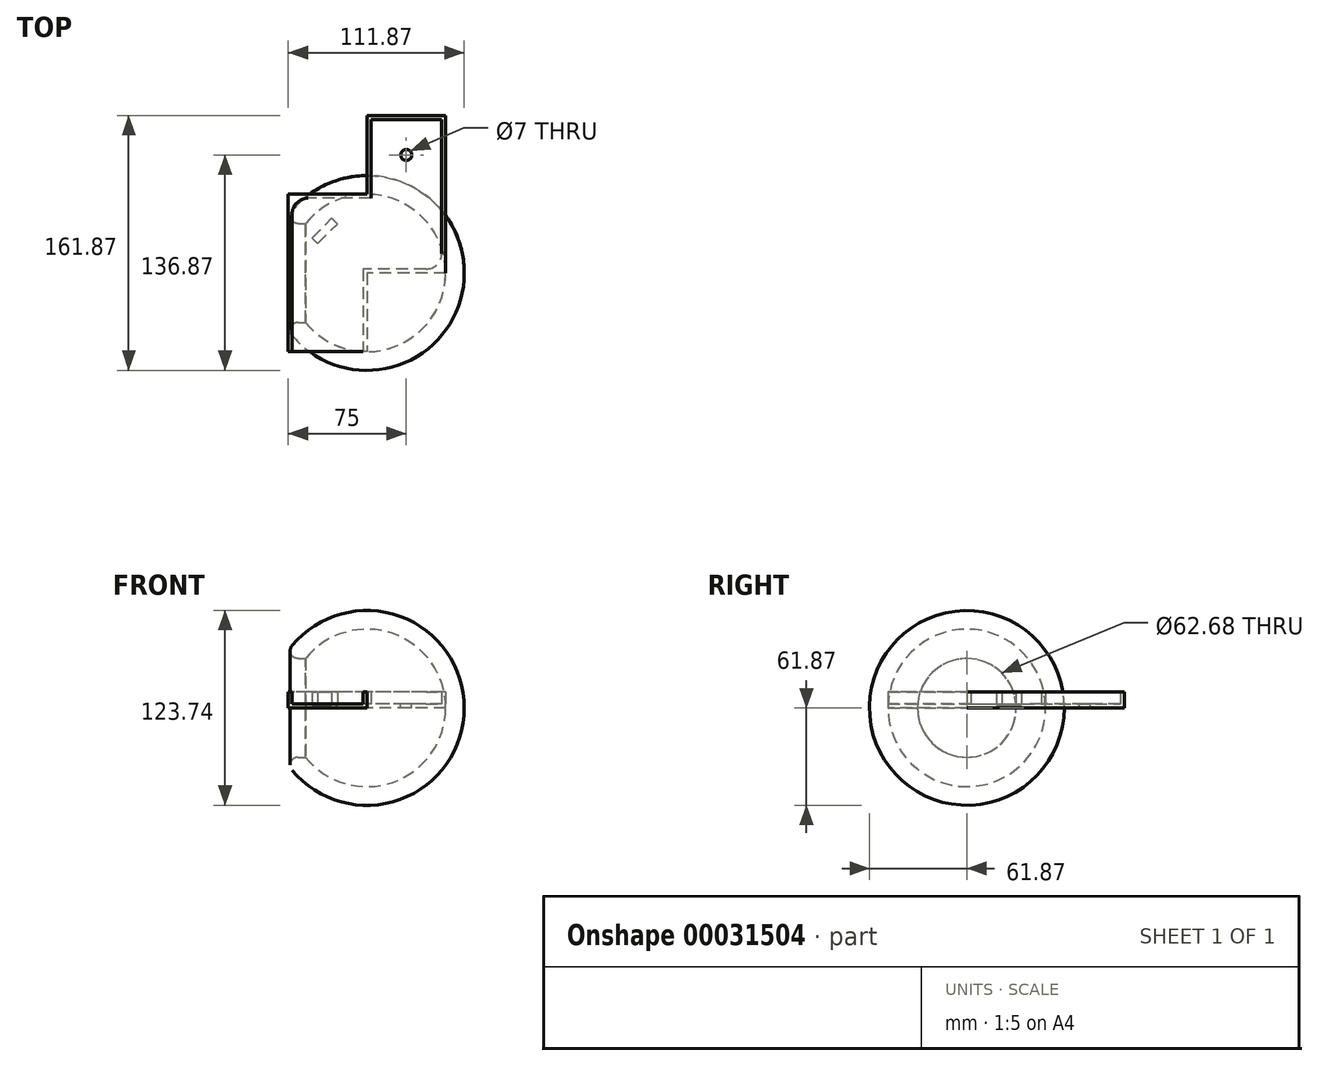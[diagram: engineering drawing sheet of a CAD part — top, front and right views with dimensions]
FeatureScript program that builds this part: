
annotation { "Feature Type Name" : "Feature", "Feature Type Description" : "" }
export const myFeature = defineFeature(function(context is Context, id is Id, definition is map)
    precondition{}
    {
        {
            var Q0;
            Q0=qCreatedBy(makeId("Top.planeOp"),FACE);
            var sketch = newSketch(context, id + "F0", { "sketchPlane" : qUnion([Q0])});
            skLineSegment(sketch, "E0", {"start": v(0, 0) * mm, "end": v(0, 50) * mm});
            skLineSegment(sketch, "E1", {"start": v(0, 50) * mm, "end": v(-50, 50) * mm});
            skLineSegment(sketch, "E2", {"start": v(-50, 50) * mm, "end": v(-50, 0) * mm});
            skLineSegment(sketch, "E3", {"start": v(-50, 0) * mm, "end": v(0, 0) * mm});
            skLineSegment(sketch, "E4", {"start": v(0, 0) * mm, "end": v(0, -50) * mm});
            skLineSegment(sketch, "E5", {"start": v(0, -50) * mm, "end": v(-50, -50) * mm});
            skLineSegment(sketch, "E6", {"start": v(-50, -50) * mm, "end": v(-50, 0) * mm});
            skLineSegment(sketch, "E7", {"start": v(0, 50) * mm, "end": v(50, 50) * mm});
            skLineSegment(sketch, "E8", {"start": v(50, 50) * mm, "end": v(50, 0) * mm});
            skLineSegment(sketch, "E9", {"start": v(50, 0) * mm, "end": v(0, 0) * mm});
            skLineSegment(sketch, "E10", {"start": v(50, 50) * mm, "end": v(50, 100) * mm});
            skLineSegment(sketch, "E11", {"start": v(50, 100) * mm, "end": v(0, 100) * mm});
            skLineSegment(sketch, "E12", {"start": v(0, 100) * mm, "end": v(0, 50) * mm});
            skSolve(sketch);
        }
        {
            var Q0;
            Q0 = qSketchRegion(id + "F0", true);
            extrude(context, id + "F1", {"entities" : qUnion([Q0]), "depth" : 10 * mm});
        }
        {
            var Q0;
            Q0=makeQuery(id+"F1.opExtrude","CAP_FACE",FACE,{"disambiguationData":[OSD([sQuery(id+"F0.wireOp",EDGE,"E1"),sQuery(id+"F0.wireOp",EDGE,"E2"),sQuery(id+"F0.wireOp",EDGE,"E4"),sQuery(id+"F0.wireOp",EDGE,"E5"),sQuery(id+"F0.wireOp",EDGE,"E6"),sQuery(id+"F0.wireOp",EDGE,"E8"),sQuery(id+"F0.wireOp",EDGE,"E9"),sQuery(id+"F0.wireOp",EDGE,"E10"),sQuery(id+"F0.wireOp",EDGE,"E11"),sQuery(id+"F0.wireOp",EDGE,"E12")])],"isStart":false});
            var Q1;
            Q1=makeQuery(id+"F1.opExtrude","SWEPT_FACE",FACE,{"disambiguationData":[OSD([sQuery(id+"F0.wireOp",EDGE,"E5")])]});
            shell(context, id + "F2", {"entities" : qUnion([Q0, Q1]), "thickness" : 2.5 * mm});
        }
        {
            var Q0;
            Q0=qCreatedBy(makeId("Top.planeOp"),FACE);
            cPlane(context, id + "F3", {"entities" : qUnion([Q0]), "cplaneType" : CPlaneType.OFFSET, "offset" : 2 * mm, "width" : 150 * mm, "height" : 150 * mm});
        }
        {
            var Q0;
            Q0=qCreatedBy(id+"F3.planeOp",FACE);
            var sketch = newSketch(context, id + "F4", { "sketchPlane" : qUnion([Q0])});
            skLineSegment(sketch, "E13", {"start": v(0, 0) * mm, "end": v(-50, 0) * mm});
            skLineSegment(sketch, "E14", {"start": v(-50, 0) * mm, "end": v(-50, 30) * mm});
            skLineSegment(sketch, "E15", {"start": v(-30, 50) * mm, "end": v(0, 50) * mm});
            skLineSegment(sketch, "E16", {"start": v(0, 50) * mm, "end": v(0, 0) * mm});
            skPoint(sketch, "E17.visualSharp", {"position": v(-50, 50) * mm});
            skArc(sketch, "E17.filletArc", {"start": v(-30, 50) * mm, "mid": v(-44.14, 44.14) * mm, "end": v(-50, 30) * mm});
            skLineSegment(sketch, "E18", {"start": v(-30, 50) * mm, "end": v(-50, 50) * mm});
            skLineSegment(sketch, "E19", {"start": v(-50, 30) * mm, "end": v(-50, 50) * mm});
            skLineSegment(sketch, "E20", {"start": v(-50, 0) * mm, "end": v(-37.5, 12.5) * mm});
            skLineSegment(sketch, "E21", {"start": v(-25, 25) * mm, "end": v(-18.75, 31.25) * mm});
            skLineSegment(sketch, "E22", {"start": v(-12.5, 37.5) * mm, "end": v(0, 50) * mm});
            skLineSegment(sketch, "E23", {"start": v(-37.5, 12.5) * mm, "end": v(-31.25, 18.75) * mm});
            skLineSegment(sketch, "E24.0", {"start": v(-28.54, 28.54) * mm, "end": v(-22.29, 34.79) * mm});
            skLineSegment(sketch, "E24.1", {"start": v(-41.04, 16.04) * mm, "end": v(-34.79, 22.29) * mm});
            skLineSegment(sketch, "E25", {"start": v(-41.04, 16.04) * mm, "end": v(-37.5, 12.5) * mm});
            skLineSegment(sketch, "E26", {"start": v(-16.04, 41.04) * mm, "end": v(-12.5, 37.5) * mm});
            skLineSegment(sketch, "E27", {"start": v(0, 0) * mm, "end": v(25, 0) * mm});
            skLineSegment(sketch, "E28", {"start": v(25, 0) * mm, "end": v(25, 75) * mm});
            skCircle(sketch, "E29", {"center": v(25, 75) * mm, "radius": 3.5 * mm});
            skLineSegment(sketch, "E30", {"start": v(-31.25, 18.75) * mm, "end": v(-25, 25) * mm});
            skLineSegment(sketch, "E31", {"start": v(-34.79, 22.29) * mm, "end": v(-28.54, 28.54) * mm});
            skLineSegment(sketch, "E32", {"start": v(-22.29, 34.79) * mm, "end": v(-16.04, 41.04) * mm});
            skLineSegment(sketch, "E33", {"start": v(-18.75, 31.25) * mm, "end": v(-12.5, 37.5) * mm});
            skLineSegment(sketch, "E34", {"start": v(-18.75, 31.25) * mm, "end": v(-22.29, 34.79) * mm});
            skLineSegment(sketch, "E35", {"start": v(-31.25, 18.75) * mm, "end": v(-34.79, 22.29) * mm});
            skSolve(sketch);
        }
        {
            var Q0;
            Q0=makeQuery(id+"F4.imprint","IMPRINT",FACE,{"disambiguationData":[TD([[makeQuery(id+"F4.imprint","IMPRINT",EDGE,{"derivedFrom":sQuery(id+"F4.wireOp",EDGE,"E21")}),1.0]])]});
            extrude(context, id + "F5", {"entities" : qUnion([Q0]), "depth" : 8 * mm});
        }
        {
            var Q0;
            Q0=makeQuery(id+"F2.opShell","OFFSET_EDGE",EDGE,{"disambiguationData":[OSD([sQuery(id+"F0.wireOp",EDGE,"E1"),sQuery(id+"F0.wireOp",EDGE,"E2")])]});
            var Q1;
            Q1=makeQuery(id+"F2.opShell","OFFSET_EDGE",EDGE,{"disambiguationData":[OSD([sQuery(id+"F0.wireOp",EDGE,"E8"),sQuery(id+"F0.wireOp",EDGE,"E9")])]});
            fillet(context, id + "F6", {"entities" : qUnion([Q0, Q1]), "radius" : 10 * mm, "tangentPropagation" : true, "allowEdgeOverflow" : false});
        }
        {
            var Q0;
            Q0=makeQuery(id+"F4.imprint","IMPRINT",FACE,{"disambiguationData":[TD([[makeQuery(id+"F4.imprint","IMPRINT",EDGE,{"derivedFrom":sQuery(id+"F4.wireOp",EDGE,"E29")}),1.0]])]});
            extrude(context, id + "F7", {"entities" : qUnion([Q0]), "operationType" : NewBodyOperationType.REMOVE, "oppositeDirection" : true, "depth" : 25 * mm, "symmetric" : true});
        }
        {
            var Q0;
            Q0=qCreatedBy(makeId("Top.planeOp"),FACE);
            var sketch = newSketch(context, id + "F8", { "sketchPlane" : qUnion([Q0])});
            skCircle(sketch, "E36", {"center": v(0, 0) * mm, "radius": 50 * mm});
            skCircle(sketch, "E37", {"center": v(0, 0) * mm, "radius": 61.87 * mm});
            skLineSegment(sketch, "E38.bottom", {"start": v(0, 0) * mm, "end": v(-113.38, 0) * mm});
            skLineSegment(sketch, "E38.top", {"start": v(0, 31.34) * mm, "end": v(-113.38, 31.34) * mm});
            skLineSegment(sketch, "E38.left", {"start": v(0, 0) * mm, "end": v(0, 31.34) * mm});
            skLineSegment(sketch, "E38.right", {"start": v(-113.38, 0) * mm, "end": v(-113.38, 31.34) * mm});
            skLineSegment(sketch, "E39", {"start": v(0, 0) * mm, "end": v(50, 0) * mm});
            skLineSegment(sketch, "E40", {"start": v(50, 0) * mm, "end": v(61.87, 0) * mm});
            skSolve(sketch);
        }
        {
            var Q0;
            {var subQ0=sQuery(id+"F8.wireOp",EDGE,"E40");Q0=makeQuery(id+"F8.imprint","IMPRINT",FACE,{"disambiguationData":[TD([[makeQuery(id+"F8.imprint","IMPRINT",EDGE,{"derivedFrom":subQ0}),1.0]])]});}
            var Q1;
            Q1=sQuery(id+"F8.wireOp",EDGE,"E38.bottom");
            revolve(context, id + "F9", {"entities" : qUnion([Q0]), "axis" : qUnion([Q1]), "revolveType" : RevolveType.FULL});
        }
        {
            var Q0;
            Q0=makeQuery(id+"F9.opRevolve","SWEPT_EDGE",EDGE,{"disambiguationData":[OSD([sQuery(id+"F8.wireOp",EDGE,"E37"),sQuery(id+"F8.wireOp",EDGE,"E38.top")])]});
            fillet(context, id + "F10", {"entities" : qUnion([Q0]), "radius" : 5 * mm, "tangentPropagation" : true, "allowEdgeOverflow" : false});
        }
    });
